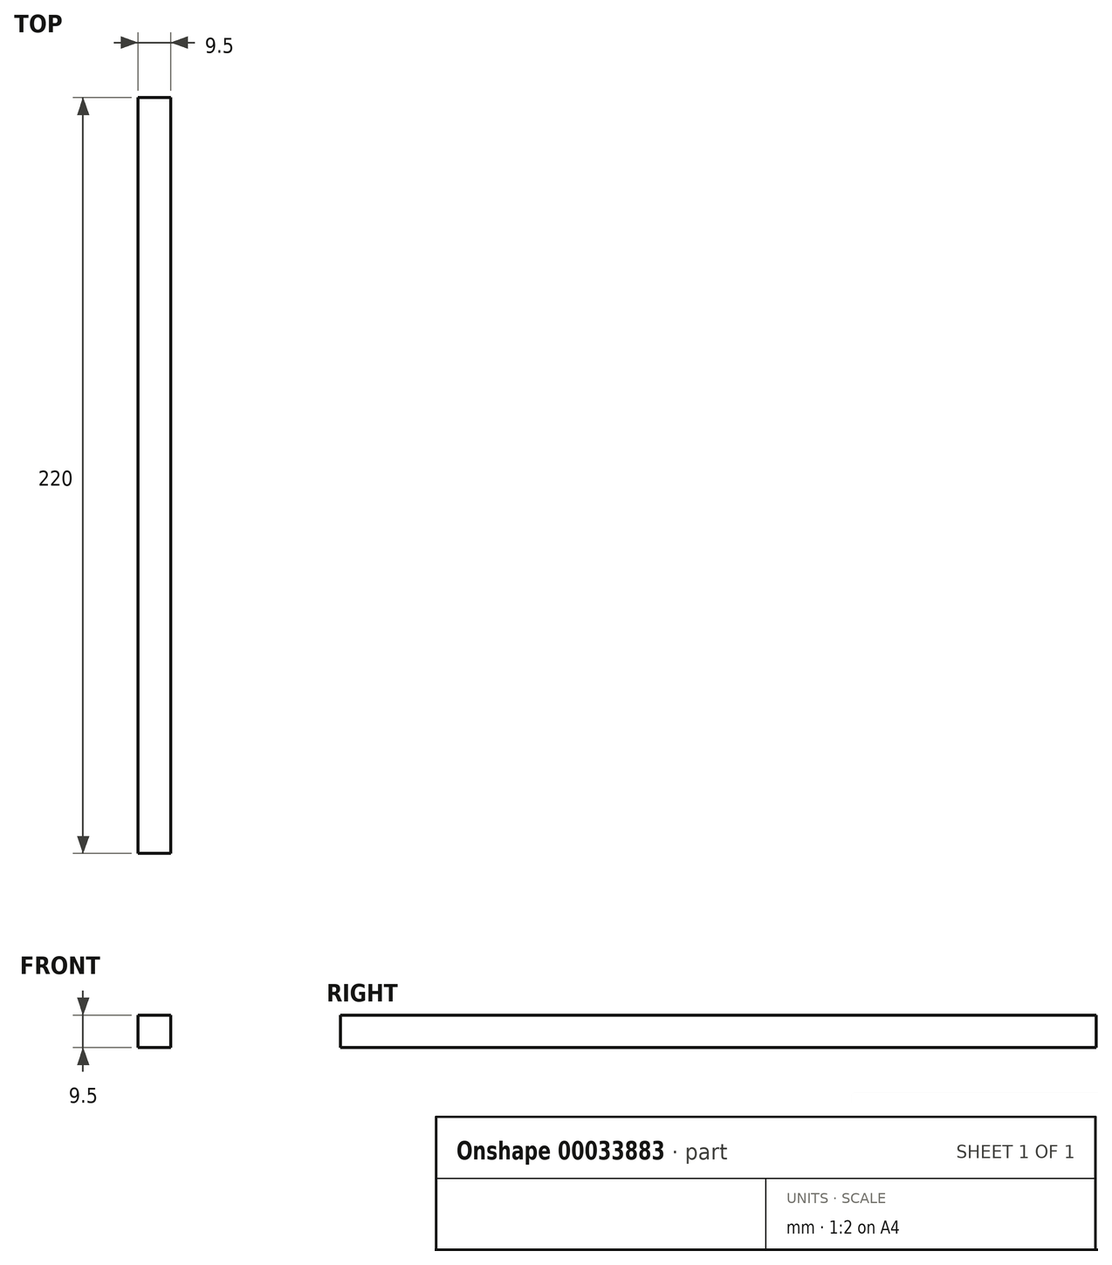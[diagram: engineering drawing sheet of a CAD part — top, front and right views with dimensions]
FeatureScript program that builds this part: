
annotation { "Feature Type Name" : "Feature", "Feature Type Description" : "" }
export const myFeature = defineFeature(function(context is Context, id is Id, definition is map)
    precondition{}
    {
        {
            var Q0;
            Q0=qCreatedBy(makeId("Front.planeOp"),FACE);
            var sketch = newSketch(context, id + "F0", { "sketchPlane" : qUnion([Q0])});
            skLineSegment(sketch, "E0.bottom", {"start": v(-42.98, 32.26) * mm, "end": v(-33.48, 32.26) * mm});
            skLineSegment(sketch, "E0.top", {"start": v(-42.98, 22.76) * mm, "end": v(-33.48, 22.76) * mm});
            skLineSegment(sketch, "E0.left", {"start": v(-42.98, 32.26) * mm, "end": v(-42.98, 22.76) * mm});
            skLineSegment(sketch, "E0.right", {"start": v(-33.48, 32.26) * mm, "end": v(-33.48, 22.76) * mm});
            skSolve(sketch);
        }
        {
            var Q0;
            Q0 = qSketchRegion(id + "F0", true);
            extrude(context, id + "F1", {"entities" : qUnion([Q0]), "oppositeDirection" : true, "depth" : 220 * mm});
        }
    });
